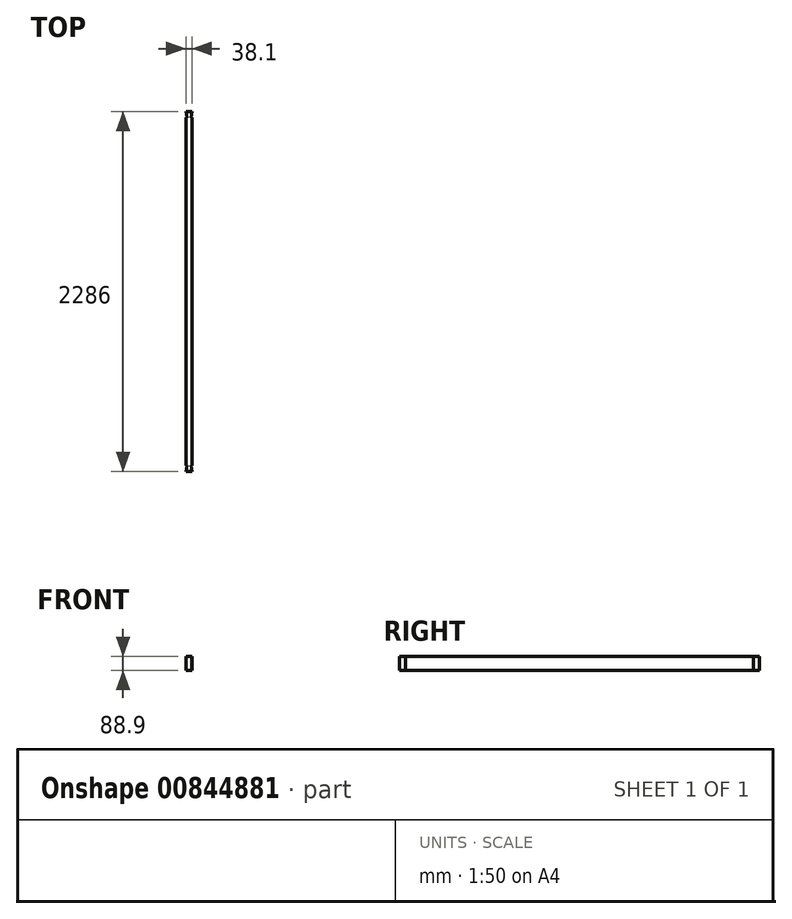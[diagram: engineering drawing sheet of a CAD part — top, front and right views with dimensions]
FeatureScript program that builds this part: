
annotation { "Feature Type Name" : "Feature", "Feature Type Description" : "" }
export const myFeature = defineFeature(function(context is Context, id is Id, definition is map)
    precondition{}
    {
        {
            var Q0;
            Q0=qCreatedBy(makeId("Front.planeOp"),FACE);
            var sketch = newSketch(context, id + "F0", { "sketchPlane" : qUnion([Q0])});
            skLineSegment(sketch, "E0.bottom", {"start": v(0, 0) * mm, "end": v(38.1, 0) * mm});
            skLineSegment(sketch, "E0.top", {"start": v(0, 88.9) * mm, "end": v(38.1, 88.9) * mm});
            skLineSegment(sketch, "E0.left", {"start": v(0, 0) * mm, "end": v(0, 88.9) * mm});
            skLineSegment(sketch, "E0.right", {"start": v(38.1, 0) * mm, "end": v(38.1, 88.9) * mm});
            skSolve(sketch);
        }
        {
            var Q0;
            Q0=makeQuery(id+"F0.imprint","IMPRINT",FACE,{"disambiguationData":[TD([[makeQuery(id+"F0.imprint","IMPRINT",EDGE,{"derivedFrom":sQuery(id+"F0.wireOp",EDGE,"E0.bottom")}),1.0]])]});
            extrude(context, id + "F1", {"entities" : qUnion([Q0]), "depth" : 2209.8 * mm, "offsetDistance" : 25.4 * mm});
        }
        {
            var Q0;
            Q0=makeQuery(id+"F1.opExtrude","SWEPT_FACE",FACE,{"disambiguationData":[OSD([sQuery(id+"F0.wireOp",EDGE,"E0.top")])]});
            var sketch = newSketch(context, id + "F2", { "sketchPlane" : qUnion([Q0])});
            skLineSegment(sketch, "E1", {"start": v(6.35, 0) * mm, "end": v(0, 38.1) * mm});
            skLineSegment(sketch, "E2", {"start": v(0, 38.1) * mm, "end": v(38.1, 38.1) * mm});
            skLineSegment(sketch, "E3", {"start": v(38.1, 38.1) * mm, "end": v(31.75, 0) * mm});
            skLineSegment(sketch, "E4", {"start": v(6.35, -2209.8) * mm, "end": v(0, -2247.9) * mm});
            skLineSegment(sketch, "E5", {"start": v(0, -2247.9) * mm, "end": v(38.1, -2247.9) * mm});
            skLineSegment(sketch, "E6", {"start": v(38.1, -2247.9) * mm, "end": v(31.75, -2209.8) * mm});
            skSolve(sketch);
        }
        {
            var Q0;
            {var subQ0=sQuery(id+"F2.wireOp",EDGE,"E1");Q0=makeQuery(id+"F2.imprint","IMPRINT",FACE,{"disambiguationData":[TD([[makeQuery(id+"F2.imprint","IMPRINT",EDGE,{"derivedFrom":subQ0}),-1.0]])]});}
            var Q1;
            {var subQ0=sQuery(id+"F2.wireOp",EDGE,"E4");Q1=makeQuery(id+"F2.imprint","IMPRINT",FACE,{"disambiguationData":[TD([[makeQuery(id+"F2.imprint","IMPRINT",EDGE,{"derivedFrom":subQ0}),1.0]])]});}
            var Q2;
            Q2=makeQuery(id+"F1.opExtrude","SWEPT_FACE",FACE,{"disambiguationData":[OSD([sQuery(id+"F0.wireOp",EDGE,"E0.bottom")])]});
            extrude(context, id + "F3", {"entities" : qUnion([Q0, Q1]), "operationType" : NewBodyOperationType.ADD, "endBound" : BoundingType.UP_TO_SURFACE, "oppositeDirection" : true, "depth" : 25.4 * mm, "endBoundEntityFace" : qUnion([Q2]), "offsetDistance" : 25.4 * mm});
        }
    });
